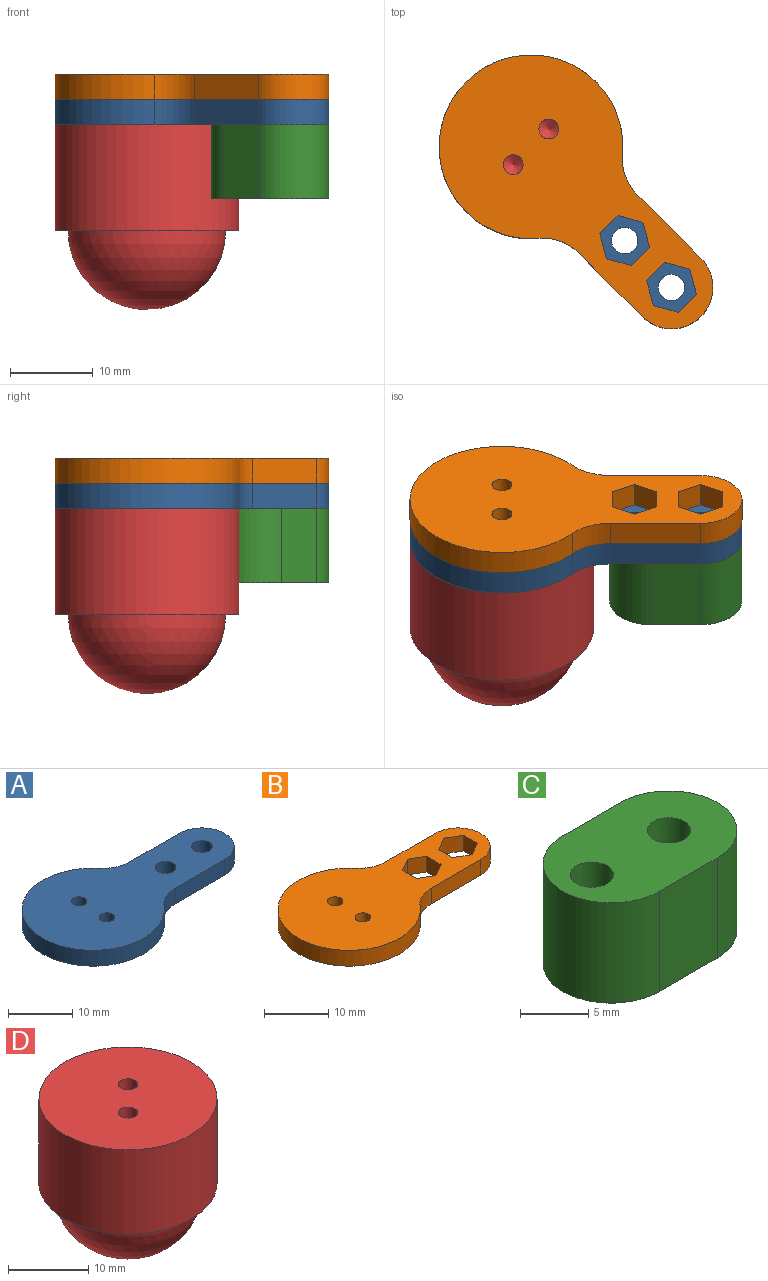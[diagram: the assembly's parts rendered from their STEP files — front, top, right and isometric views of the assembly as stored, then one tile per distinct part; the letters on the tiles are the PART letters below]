
ASSEMBLY  parts=4 mates=10
PART A: 12 faces, bbox 40.1x22.2x3 mm
  f0: cylinder r=5mm len=10mm, axis (0,0,-1), area 47.1mm2, adj f1,f3,f4,f5
  f1: plane 10.91x3mm, normal (0,1,0), area 32.7mm2, adj f0,f4,f5,f10
  f2: cylinder r=11.1mm len=22.2mm, axis (0,0,-1), area 162.7mm2, adj f4,f5,f10,f11
  f3: plane 10.91x3mm, normal (0,-1,0), area 32.7mm2, adj f0,f4,f5,f11
  f4: plane 40.1x22.2mm, normal (0,0,1), area 536.8mm2, adj f0,f1,f2,f3,f6,f7,f8,f9
  f5: plane 40.1x22.2mm, normal (0,0,-1), area 536.8mm2, adj f0,f1,f2,f3,f6,f7,f8,f9
  f6: cylinder r=1.6mm len=3.2mm, axis (0,0,-1), area 30.2mm2, adj f4,f5
  f7: cylinder r=1.6mm len=3.2mm, axis (0,0,-1), area 30.2mm2, adj f4,f5
  f8: cylinder r=1.2mm len=3mm, axis (0,0,-1), area 22.6mm2, adj f4,f5
  f9: cylinder r=1.2mm len=3mm, axis (0,0,-1), area 22.6mm2, adj f4,f5
  f10: cylinder r=6mm len=4.59mm, axis (0,0,-1), area 15.7mm2, adj f1,f2,f4,f5
  f11: cylinder r=6mm len=4.59mm, axis (0,0,-1), area 15.7mm2, adj f2,f3,f4,f5
PART B: 22 faces, bbox 40.1x22.2x3 mm
  f0: plane 3.12x3mm, normal (-1,0,0), area 9.4mm2, adj f1,f15,f16,f17
  f1: plane 3x2.7mm, normal (-0.5,0.87,0), area 9.4mm2, adj f0,f2,f16,f17
  f2: plane 3x2.7mm, normal (0.5,0.87,0), area 9.4mm2, adj f1,f3,f16,f17
  f3: plane 3.12x3mm, normal (1,0,0), area 9.4mm2, adj f2,f4,f16,f17
  f4: plane 3x2.7mm, normal (0.5,-0.87,0), area 9.4mm2, adj f3,f15,f16,f17
  f5: cylinder r=5mm len=10mm, axis (0,0,-1), area 47.1mm2, adj f6,f13,f16,f17
  f6: plane 10.91x3mm, normal (0,1,0), area 32.7mm2, adj f5,f16,f17,f20
  f7: cylinder r=11.1mm len=22.2mm, axis (0,0,-1), area 162.7mm2, adj f16,f17,f20,f21
  f8: plane 3.12x3mm, normal (1,0,0), area 9.4mm2, adj f9,f14,f16,f17
  f9: plane 3x2.7mm, normal (0.5,-0.87,0), area 9.4mm2, adj f8,f10,f16,f17
  f10: plane 3x2.7mm, normal (-0.5,-0.87,0), area 9.4mm2, adj f9,f11,f16,f17
  f11: plane 3.12x3mm, normal (-1,0,0), area 9.4mm2, adj f10,f12,f16,f17
  f12: plane 3x2.7mm, normal (-0.5,0.87,0), area 9.4mm2, adj f11,f14,f16,f17
  f13: plane 10.91x3mm, normal (0,-1,0), area 32.7mm2, adj f5,f16,f17,f21
  f14: plane 3x2.7mm, normal (0.5,0.87,0), area 9.4mm2, adj f8,f12,f16,f17
  f15: plane 3x2.7mm, normal (-0.5,-0.87,0), area 9.4mm2, adj f0,f4,f16,f17
  f16: plane 40.1x22.2mm, normal (0,0,1), area 502.4mm2, adj f0,f1,f2,f3,f4,f5,f6,f7
  f17: plane 40.1x22.2mm, normal (0,0,-1), area 502.4mm2, adj f0,f1,f2,f3,f4,f5,f6,f7
  f18: cylinder r=1.2mm len=3mm, axis (0,0,-1), area 22.6mm2, adj f16,f17
  f19: cylinder r=1.2mm len=3mm, axis (0,0,-1), area 22.6mm2, adj f16,f17
  f20: cylinder r=6mm len=4.59mm, axis (0,0,-1), area 15.7mm2, adj f6,f7,f16,f17
  f21: cylinder r=6mm len=4.59mm, axis (0,0,-1), area 15.7mm2, adj f7,f13,f16,f17
PART C: 8 faces, bbox 16x10x9 mm
  f0: plane 9x6mm, normal (0,-1,0), area 54mm2, adj f1,f3,f4,f5
  f1: cylinder r=5mm len=10mm, axis (0,0,-1), area 141.4mm2, adj f0,f2,f4,f5
  f2: plane 9x6mm, normal (0,1,0), area 54mm2, adj f1,f3,f4,f5
  f3: cylinder r=5mm len=10mm, axis (0,0,-1), area 141.4mm2, adj f0,f2,f4,f5
  f4: plane 16x10mm, normal (0,0,1), area 122.5mm2, adj f0,f1,f2,f3,f6,f7
  f5: plane 16x10mm, normal (0,0,-1), area 122.5mm2, adj f0,f1,f2,f3,f6,f7
  f6: cylinder r=1.6mm len=9mm, axis (0,0,-1), area 90.5mm2, adj f4,f5
  f7: cylinder r=1.6mm len=9mm, axis (0,0,-1), area 90.5mm2, adj f4,f5
PART D: 8 faces, bbox 22.2x22.2x22.4 mm
  f0: plane 22.2x22.2mm, normal (0,0,1), area 378mm2, adj f1,f5,f7
  f1: cylinder r=11.1mm len=22.2mm, axis (0,0,-1), area 897.9mm2, adj f0,f2
  f2: plane 22.2x22.2mm, normal (0,0,-1), area 102.1mm2, adj f1,f3
  f3: sphere r=9.53mm, area 570mm2, adj f2
  f4: cone r=0mm half-angle=59deg, axis (0,0,1), area 5.3mm2, adj f5
  f5: cylinder r=1.2mm len=4.5mm, axis (0,0,1), area 33.9mm2, adj f0,f4
  f6: cone r=0mm half-angle=59deg, axis (0,0,1), area 5.3mm2, adj f7
  f7: cylinder r=1.2mm len=4.5mm, axis (0,0,1), area 33.9mm2, adj f0,f6
PLACE A rot(axis=(0,0,-1),45deg) t=(-0.16,-0.03,0.04)mm
PLACE B rot(axis=(0,0,-1),45deg) t=(-0.16,-0.03,3.04)mm
PLACE C rot(axis=(0,0,-1),45deg) t=(16.81,-17,-8.96)mm
PLACE D t=(-0.16,-0.03,-22.36)mm fixed
MATE cylindrical D.f4 <-> B.f19  axis (0,0,1) through (-2.31,-2.19,0.04)mm
MATE planar A.f5 <-> D.f1  axis (0,0,-1) through (3.85,-4.03,0.04)mm
MATE planar A.f5 <-> C.f4  axis (0,0,-1) through (9.42,-16.68,0.04)mm
MATE cylindrical A.f8 <-> D.f4  axis (0,0,-1) through (-2.31,-2.19,3.04)mm
MATE cylindrical D.f6 <-> A.f9  axis (0,0,1) through (2,2.13,-2.21)mm
MATE cylindrical A.f7 <-> C.f6  axis (0,0,-1) through (11.16,-11.34,1.54)mm
MATE cylindrical D.f6 <-> A.f9  axis (0,0,1) through (2,2.13,0.04)mm
MATE planar B.f17 <-> A.f4  axis (0,0,-1) through (3.15,-3.34,3.04)mm
MATE cylindrical C.f7 <-> A.f0  axis (0,0,-1) through (16.81,-17,-8.96)mm
MATE cylindrical B.f18 <-> D.f6  axis (0,0,-1) through (2,2.13,4.54)mm
